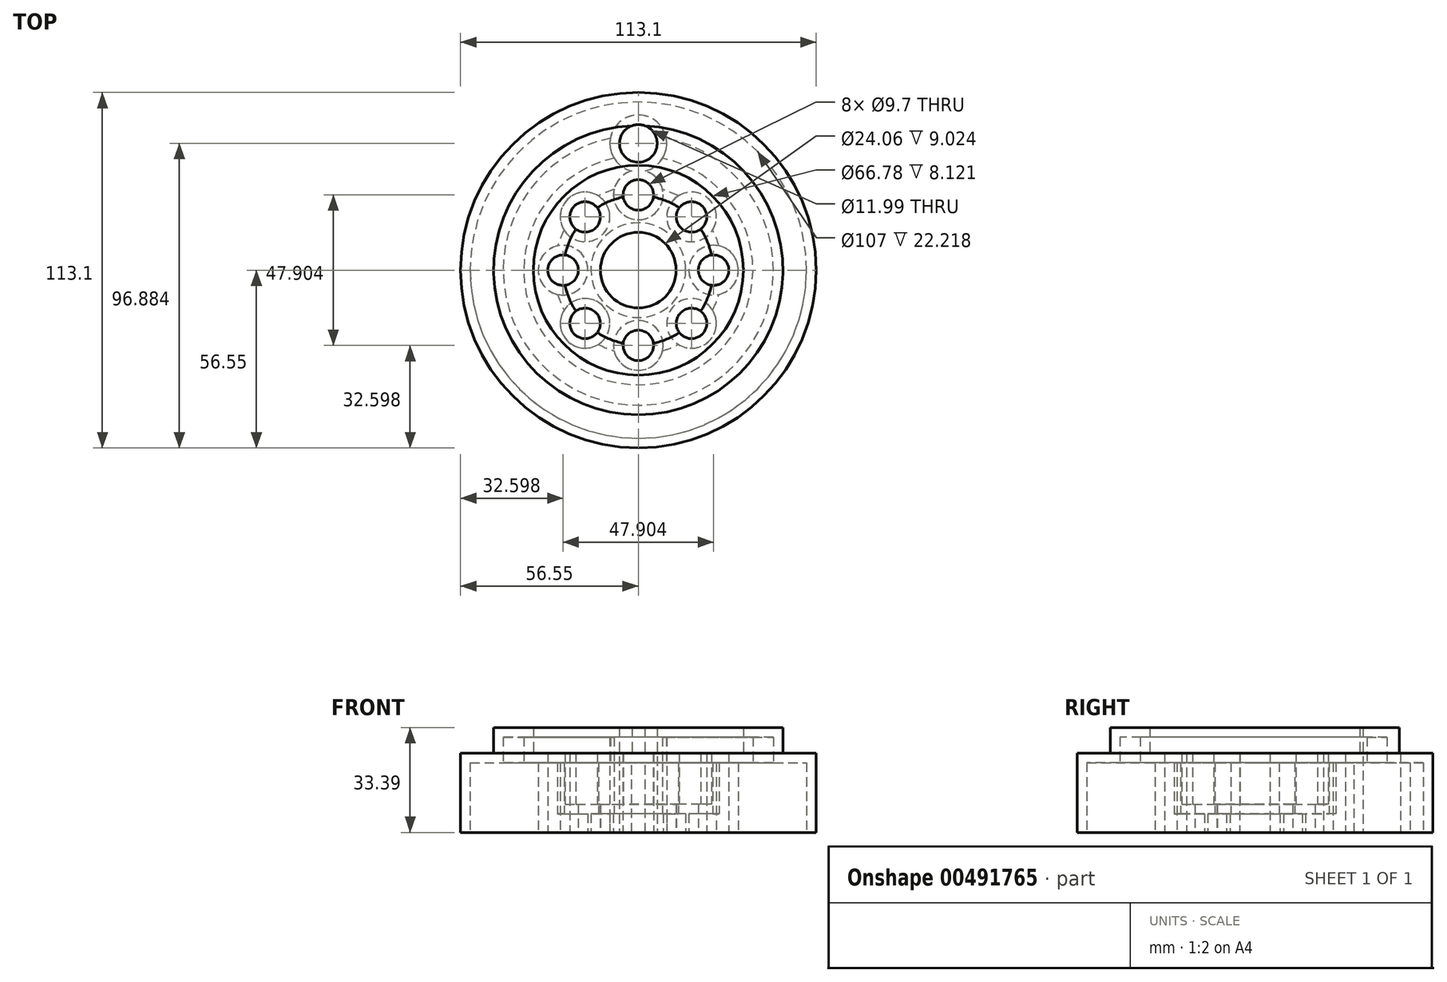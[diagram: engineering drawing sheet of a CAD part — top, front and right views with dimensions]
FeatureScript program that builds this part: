
annotation { "Feature Type Name" : "Feature", "Feature Type Description" : "" }
export const myFeature = defineFeature(function(context is Context, id is Id, definition is map)
    precondition{}
    {
        {
            var Q0;
            Q0=qCreatedBy(makeId("Front.planeOp"),FACE);
            var sketch = newSketch(context, id + "F0", { "sketchPlane" : qUnion([Q0])});
            skLineSegment(sketch, "E0", {"start": v(0, 0) * mm, "end": v(0, 25.27) * mm, "construction": true});
            skLineSegment(sketch, "E1.bottom", {"start": v(23.76, 0) * mm, "end": v(56.55, 0) * mm});
            skLineSegment(sketch, "E1.top", {"start": v(23.76, 25.27) * mm, "end": v(33.39, 25.27) * mm});
            skLineSegment(sketch, "E1.left", {"start": v(23.76, 9.02) * mm, "end": v(23.76, 25.27) * mm});
            skLineSegment(sketch, "E1.right", {"start": v(56.55, 0) * mm, "end": v(56.55, 25.27) * mm});
            skLineSegment(sketch, "E2.bottom", {"start": v(23.76, 0) * mm, "end": v(12.03, 0) * mm});
            skLineSegment(sketch, "E2.top", {"start": v(23.76, 9.02) * mm, "end": v(12.03, 9.02) * mm});
            skLineSegment(sketch, "E2.right", {"start": v(12.03, 0) * mm, "end": v(12.03, 9.02) * mm});
            skLineSegment(sketch, "E3.top", {"start": v(33.39, 33.39) * mm, "end": v(46.02, 33.39) * mm});
            skLineSegment(sketch, "E3.left", {"start": v(33.39, 25.27) * mm, "end": v(33.39, 33.39) * mm});
            skLineSegment(sketch, "E3.right", {"start": v(46.02, 25.27) * mm, "end": v(46.02, 33.39) * mm});
            skLineSegment(sketch, "E4.trimOffspring", {"start": v(46.02, 25.27) * mm, "end": v(56.55, 25.27) * mm});
            skSolve(sketch);
        }
        {
            var Q0;
            Q0 = qSketchRegion(id + "F0", true);
            var Q1;
            Q1=sQuery(id+"F0.wireOp",EDGE,"E0");
            revolve(context, id + "F1", {"entities" : qUnion([Q0]), "axis" : qUnion([Q1]), "revolveType" : RevolveType.FULL});
        }
        {
            var Q0;
            Q0=makeQuery(id+"F1.opRevolve","SWEPT_FACE",FACE,{"disambiguationData":[OSD([sQuery(id+"F0.wireOp",EDGE,"E1.bottom"),sQuery(id+"F0.wireOp",EDGE,"E2.bottom")])]});
            var sketch = newSketch(context, id + "F2", { "sketchPlane" : qUnion([Q0])});
            skCircle(sketch, "E5", {"center": v(0, 0) * mm, "radius": 40.33 * mm, "construction": true});
            skCircle(sketch, "E6", {"center": v(0, -40.33) * mm, "radius": 6 * mm});
            skSolve(sketch);
        }
        {
            var Q0;
            Q0=makeQuery(id+"F2.imprint","IMPRINT",FACE,{"disambiguationData":[TD([[makeQuery(id+"F2.imprint","IMPRINT",EDGE,{"derivedFrom":sQuery(id+"F2.wireOp",EDGE,"E6")}),1.0]])]});
            extrude(context, id + "F3", {"entities" : qUnion([Q0]), "operationType" : NewBodyOperationType.REMOVE, "endBound" : BoundingType.THROUGH_ALL, "oppositeDirection" : true, "depth" : 25.4 * mm});
        }
        {
            var Q0;
            Q0=makeQuery(id+"F1.opRevolve","SWEPT_FACE",FACE,{"disambiguationData":[OSD([sQuery(id+"F0.wireOp",EDGE,"E1.bottom"),sQuery(id+"F0.wireOp",EDGE,"E2.bottom")])]});
            var sketch = newSketch(context, id + "F4", { "sketchPlane" : qUnion([Q0])});
            skCircle(sketch, "E7", {"center": v(0, 0) * mm, "radius": 23.95 * mm, "construction": true});
            skCircle(sketch, "E8", {"center": v(0, -23.95) * mm, "radius": 4.85 * mm});
            skSolve(sketch);
        }
        {
            var Q0;
            Q0=makeQuery(id+"F4.imprint","IMPRINT",FACE,{"disambiguationData":[TD([[makeQuery(id+"F4.imprint","IMPRINT",EDGE,{"derivedFrom":sQuery(id+"F4.wireOp",EDGE,"E8")}),1.0]])]});
            extrude(context, id + "F5", {"entities" : qUnion([Q0]), "operationType" : NewBodyOperationType.REMOVE, "endBound" : BoundingType.THROUGH_ALL, "oppositeDirection" : true, "depth" : 25.4 * mm});
        }
        {
            var Q0;
            Q0=makeQuery(id+"F5.boolean.opBoolean","COPY",FACE,{"derivedFrom":makeQuery(id+"F5.opExtrude","SWEPT_FACE",FACE,{"disambiguationData":[OSD([sQuery(id+"F4.wireOp",EDGE,"E8")])]})});
            var Q1;
            Q1=sQuery(id+"F4.wireOp",EDGE,"E7");
            circularPattern(context, id + "F6", {"patternType" : PatternType.FACE, "faces" : qUnion([Q0]), "axis" : qUnion([Q1]), "angle" : 360 * degree, "instanceCount" : 8, "equalSpace" : true});
        }
        {
            var Q0;
            Q0=makeQuery(id+"F1.opRevolve","SWEPT_FACE",FACE,{"disambiguationData":[OSD([sQuery(id+"F0.wireOp",EDGE,"E1.bottom"),sQuery(id+"F0.wireOp",EDGE,"E2.bottom")])]});
            shell(context, id + "F7", {"entities" : qUnion([Q0]), "thickness" : 3.05 * mm});
        }
    });
